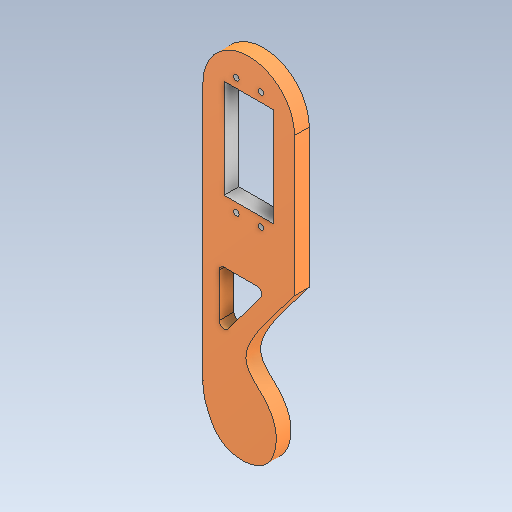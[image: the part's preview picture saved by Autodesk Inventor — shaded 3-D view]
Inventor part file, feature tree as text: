
AUTODESK INVENTOR PART (.ipt)
format: ipt  version: 2020.3 (Build 243373000, 373)  size: 216,064 bytes
history: native  units: mm
features: other x3, extrude x2, sketch x2, direct_edit x1, projected_geometry x1, move_body x1
ambient origin geometry x8: Origin, YZ Plane, XZ Plane, XY Plane, X Axis, Y Axis, Z Axis, Center Point
bodies: Solid1 (feature_tree)
feature tree (10):
  other  "Part 6.ipt"
  extrude  "Extrusion1"  Depth=10.0mm TaperAngle=0.0deg
  sketch  "Sketch2"  dims[d3=0.0mm d4=-5.25mm d5=0.0mm d6=0.0mm d7=0.0mm]
  direct_edit  "Direct Edit1"
  extrude  "Extrusion2"  TaperAngle=0.0deg  [1 undecoded]
  other  "Solid1::Part 6.ipt"
  other  "TaggingFeature1"
  sketch  "Sketch1"  dims[d0=20.0mm d1=10.0mm d2=0.0mm]
  projected_geometry  "Projected Loop1"
  move_body  "Move1"
note: 1 required parameter value undecoded (feature->parameter linkage not recoverable at this tier; creation-order binding heuristic only, values carry confidence <= 0.55)
